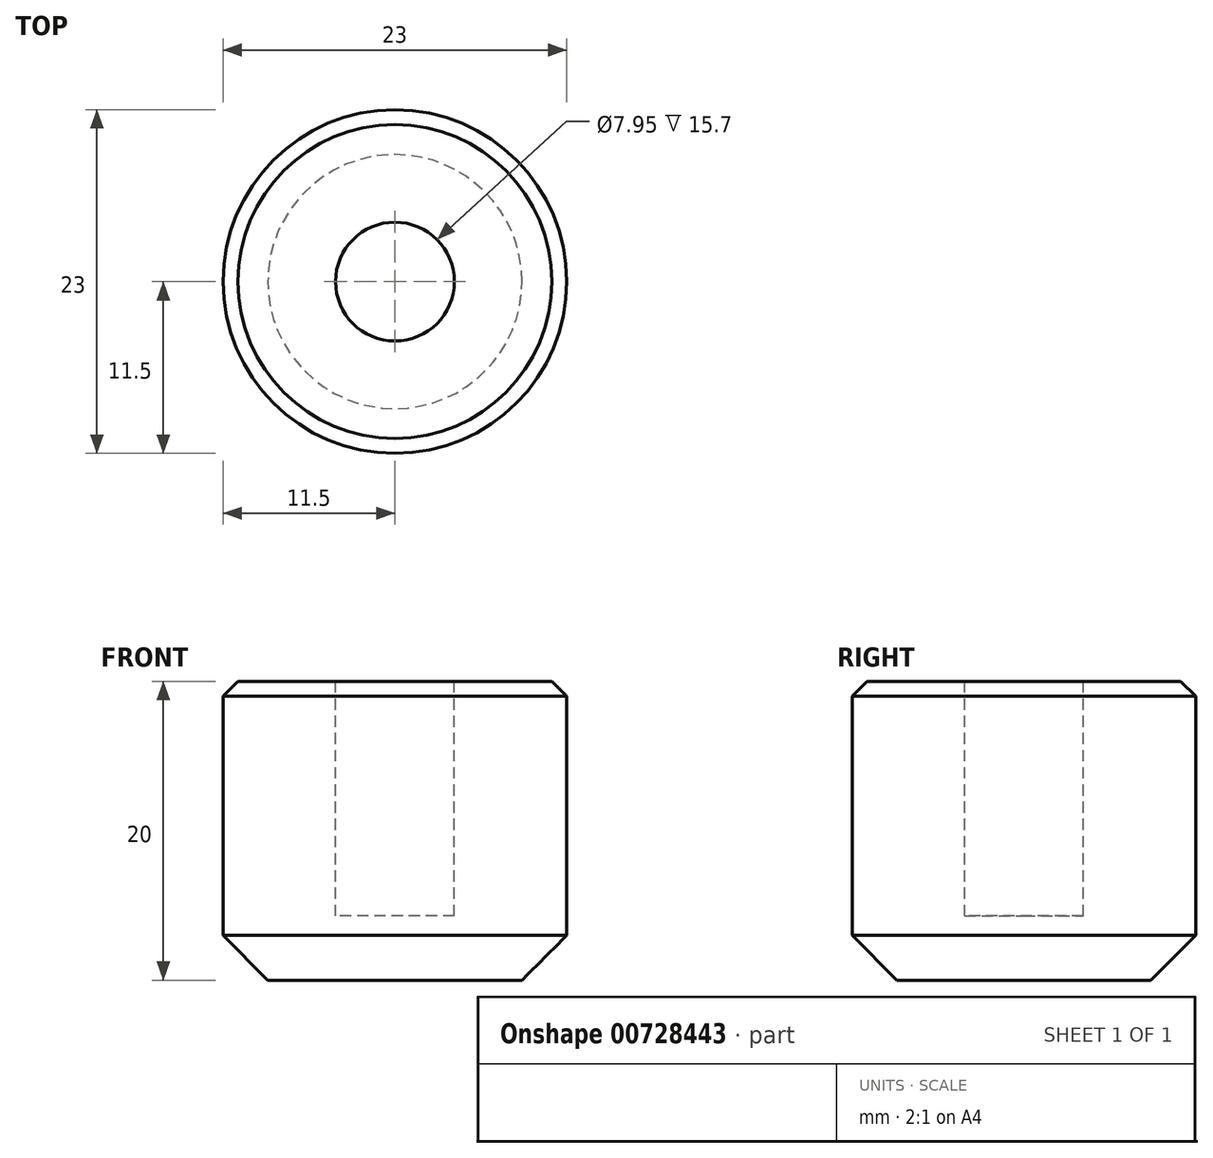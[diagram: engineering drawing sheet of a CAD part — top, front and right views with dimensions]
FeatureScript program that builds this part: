
annotation { "Feature Type Name" : "Feature", "Feature Type Description" : "" }
export const myFeature = defineFeature(function(context is Context, id is Id, definition is map)
    precondition{}
    {
        {
            var Q0;
            Q0=qCreatedBy(makeId("Top.planeOp"),FACE);
            var sketch = newSketch(context, id + "F0", { "sketchPlane" : qUnion([Q0])});
            skCircle(sketch, "E0", {"center": v(0, 0) * mm, "radius": 3.99 * mm});
            skCircle(sketch, "E1", {"center": v(0, 0) * mm, "radius": 11.5 * mm});
            skSolve(sketch);
        }
        {
            var Q0;
            Q0 = qSketchRegion(id + "F0", true);
            var Q1;
            Q1=makeQuery(id+"F0.imprint","IMPRINT",FACE,{"disambiguationData":[TD([[makeQuery(id+"F0.imprint","IMPRINT",EDGE,{"derivedFrom":sQuery(id+"F0.wireOp",EDGE,"E0")}),1.0]])]});
            extrude(context, id + "F1", {"entities" : qUnion([Q0, Q1]), "depth" : 20 * mm, "offsetDistance" : 25 * mm});
        }
        {
            var Q0;
            Q0=makeQuery(id+"F1.opExtrude","CAP_FACE",FACE,{"disambiguationData":[OSD([sQuery(id+"F0.wireOp",EDGE,"E1")])],"isStart":false});
            var sketch = newSketch(context, id + "F2", { "sketchPlane" : qUnion([Q0])});
            skCircle(sketch, "E2", {"center": v(0, 0) * mm, "radius": 3.97 * mm});
            skSolve(sketch);
        }
        {
            var Q0;
            Q0 = qSketchRegion(id + "F2", true);
            extrude(context, id + "F3", {"entities" : qUnion([Q0]), "operationType" : NewBodyOperationType.REMOVE, "oppositeDirection" : true, "depth" : 15.7 * mm, "offsetDistance" : 25 * mm});
        }
        {
            var Q0;
            Q0=makeQuery(id+"F1.opExtrude","CAP_EDGE",EDGE,{"disambiguationData":[OSD([sQuery(id+"F0.wireOp",EDGE,"E1")])],"isStart":true});
            chamfer(context, id + "F4", {"entities" : qUnion([Q0]), "width" : 3 * mm, "tangentPropagation" : true});
        }
        {
            var Q0;
            Q0=makeQuery(id+"F1.opExtrude","CAP_EDGE",EDGE,{"disambiguationData":[OSD([sQuery(id+"F0.wireOp",EDGE,"E1")])],"isStart":false});
            var Q1;
            Q1=makeQuery(id+"F3.boolean.opBoolean","COPY",EDGE,{"derivedFrom":makeQuery(id+"F3.opExtrude","CAP_EDGE",EDGE,{"disambiguationData":[OSD([sQuery(id+"F2.wireOp",EDGE,"E2")])],"isStart":true})});
            chamfer(context, id + "F5", {"entities" : qUnion([Q0, Q1]), "width" : 1 * mm, "tangentPropagation" : true});
        }
    });
